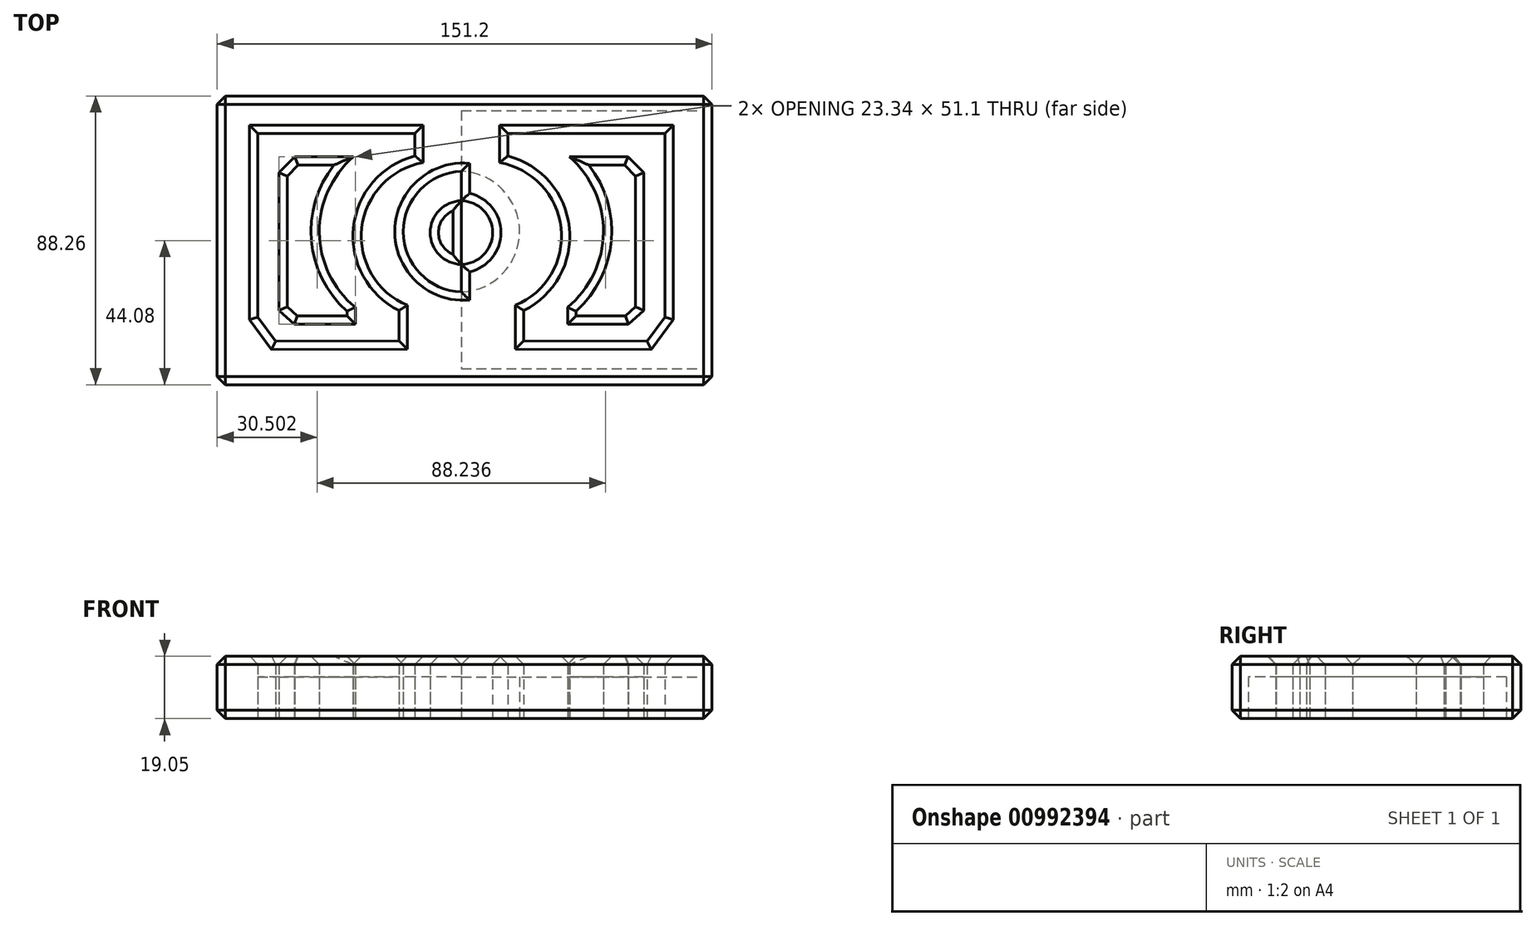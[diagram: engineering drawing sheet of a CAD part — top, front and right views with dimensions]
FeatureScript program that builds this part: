
annotation { "Feature Type Name" : "Feature", "Feature Type Description" : "" }
export const myFeature = defineFeature(function(context is Context, id is Id, definition is map)
    precondition{}
    {
        {
            var Q0;
            Q0=qCreatedBy(makeId("Top.planeOp"),FACE);
            var sketch = newSketch(context, id + "F0", { "sketchPlane" : qUnion([Q0])});
            skArc(sketch, "E0", {"start": v(0, 10.27) * mm, "mid": v(-9.53, 0.52) * mm, "end": v(0, -9.23) * mm});
            skArc(sketch, "E1", {"start": v(0, 19.24) * mm, "mid": v(-17.8, 0.8) * mm, "end": v(0, -17.63) * mm});
            skArc(sketch, "E2", {"start": v(-14.23, 23.93) * mm, "mid": v(-33, 1.98) * mm, "end": v(-19.07, -23.32) * mm});
            skArc(sketch, "E3", {"start": v(-33, 23.65) * mm, "mid": v(-43.41, 0.53) * mm, "end": v(-32.45, -22.32) * mm});
            skPoint(sketch, "E3.startSnap0", {"position": v(-33, 1.98) * mm});
            skLineSegment(sketch, "E4", {"start": v(-33, 23.65) * mm, "end": v(-50.95, 23.65) * mm});
            skLineSegment(sketch, "E5", {"start": v(-50.95, 23.65) * mm, "end": v(-55.79, 18.8) * mm});
            skLineSegment(sketch, "E6", {"start": v(-55.79, 18.8) * mm, "end": v(-55.79, 0) * mm});
            skLineSegment(sketch, "E7", {"start": v(-14.23, 23.93) * mm, "end": v(-14.23, 30.76) * mm});
            skLineSegment(sketch, "E8", {"start": v(-14.23, 30.76) * mm, "end": v(-62.2, 30.76) * mm});
            skLineSegment(sketch, "E9", {"start": v(-62.2, 30.76) * mm, "end": v(-62.2, -25.31) * mm});
            skLineSegment(sketch, "E10", {"start": v(-62.2, -25.31) * mm, "end": v(-58.64, -30.15) * mm});
            skLineSegment(sketch, "E11", {"start": v(-58.64, -30.15) * mm, "end": v(-56.78, -32.67) * mm});
            skLineSegment(sketch, "E12", {"start": v(-55.79, 0) * mm, "end": v(-55.79, -23.32) * mm});
            skLineSegment(sketch, "E13", {"start": v(-55.79, -23.32) * mm, "end": v(-51.1, -27.45) * mm});
            skLineSegment(sketch, "E14", {"start": v(-32.45, -22.32) * mm, "end": v(-32.45, -27.45) * mm});
            skLineSegment(sketch, "E15", {"start": v(0, 42.28) * mm, "end": v(0, -45.98) * mm});
            skPoint(sketch, "E15.endSnap0", {"position": v(1.57, -45.98) * mm});
            skLineSegment(sketch, "E16.MirrorCS", {"start": v(14.23, 30.76) * mm, "end": v(62.2, 30.76) * mm});
            skLineSegment(sketch, "E17.MirrorCS", {"start": v(14.23, 23.93) * mm, "end": v(14.23, 30.76) * mm});
            skArc(sketch, "E18.MirrorCS", {"start": v(14.23, 23.93) * mm, "mid": v(33, 1.98) * mm, "end": v(19.07, -23.32) * mm});
            skLineSegment(sketch, "E19.MirrorCS", {"start": v(62.2, -25.31) * mm, "end": v(58.64, -30.15) * mm});
            skLineSegment(sketch, "E20.MirrorCS", {"start": v(58.64, -30.15) * mm, "end": v(56.78, -32.67) * mm});
            skLineSegment(sketch, "E21.MirrorCS", {"start": v(62.2, 30.76) * mm, "end": v(62.2, -25.31) * mm});
            skLineSegment(sketch, "E22.MirrorCS", {"start": v(55.79, 0) * mm, "end": v(55.79, -23.32) * mm});
            skLineSegment(sketch, "E23.MirrorCS", {"start": v(55.79, 18.8) * mm, "end": v(55.79, 0) * mm});
            skLineSegment(sketch, "E24.MirrorCS", {"start": v(50.95, 23.65) * mm, "end": v(55.79, 18.8) * mm});
            skLineSegment(sketch, "E25.MirrorCS", {"start": v(33, 23.65) * mm, "end": v(50.95, 23.65) * mm});
            skArc(sketch, "E26.MirrorCS", {"start": v(33, 23.65) * mm, "mid": v(43.41, 0.53) * mm, "end": v(32.45, -22.32) * mm});
            skLineSegment(sketch, "E27.MirrorCS", {"start": v(32.45, -22.32) * mm, "end": v(32.45, -27.45) * mm});
            skLineSegment(sketch, "E28.MirrorCS", {"start": v(55.79, -23.32) * mm, "end": v(51.1, -27.45) * mm});
            skArc(sketch, "E29.MirrorCS", {"start": v(0, 19.24) * mm, "mid": v(17.8, 0.8) * mm, "end": v(0, -17.63) * mm});
            skArc(sketch, "E30.MirrorCS", {"start": v(0, 10.27) * mm, "mid": v(9.53, 0.52) * mm, "end": v(0, -9.23) * mm});
            skLineSegment(sketch, "E31.bottom", {"start": v(-70.02, 37.74) * mm, "end": v(73.73, 37.74) * mm});
            skLineSegment(sketch, "E31.top", {"start": v(-70.02, -41.11) * mm, "end": v(73.73, -41.11) * mm});
            skLineSegment(sketch, "E31.left", {"start": v(-70.02, 37.74) * mm, "end": v(-70.02, -41.11) * mm});
            skLineSegment(sketch, "E31.right", {"start": v(73.73, 37.74) * mm, "end": v(73.73, -41.11) * mm});
            skLineSegment(sketch, "E32.bottom", {"start": v(-74.62, 42.28) * mm, "end": v(76.58, 42.28) * mm});
            skLineSegment(sketch, "E32.top", {"start": v(-74.62, -45.98) * mm, "end": v(76.58, -45.98) * mm});
            skLineSegment(sketch, "E32.left", {"start": v(-74.62, 42.28) * mm, "end": v(-74.62, -45.98) * mm});
            skLineSegment(sketch, "E32.right", {"start": v(76.58, 42.28) * mm, "end": v(76.58, -45.98) * mm});
            skLineSegment(sketch, "E33", {"start": v(-51.1, -27.45) * mm, "end": v(-32.45, -27.45) * mm});
            skLineSegment(sketch, "E34", {"start": v(-19.07, -23.32) * mm, "end": v(-19.07, -32.53) * mm});
            skLineSegment(sketch, "E35", {"start": v(-19.07, -32.53) * mm, "end": v(-56.78, -32.67) * mm});
            skLineSegment(sketch, "E36.MirrorCS", {"start": v(51.1, -27.45) * mm, "end": v(32.45, -27.45) * mm});
            skLineSegment(sketch, "E37.MirrorCS", {"start": v(19.07, -32.53) * mm, "end": v(56.78, -32.67) * mm});
            skLineSegment(sketch, "E38.MirrorCS", {"start": v(19.07, -23.32) * mm, "end": v(19.07, -32.53) * mm});
            skSolve(sketch);
        }
        {
            var Q0;
            Q0=makeQuery(id+"F0.imprint","IMPRINT",FACE,{"disambiguationData":[TD([[makeQuery(id+"F0.imprint","IMPRINT",EDGE,{"derivedFrom":sQuery(id+"F0.wireOp",EDGE,"E3")}),-1.0]])]});
            var Q1;
            {var subQ5=sQuery(id+"F0.wireOp",EDGE,"E1");Q1=makeQuery(id+"F0.imprint","IMPRINT",FACE,{"disambiguationData":[TD([[makeQuery(id+"F0.imprint","IMPRINT",EDGE,{"derivedFrom":subQ5}),-1.0]])]});}
            var Q2;
            {var subQ0=sQuery(id+"F0.wireOp",EDGE,"E0");Q2=makeQuery(id+"F0.imprint","IMPRINT",FACE,{"disambiguationData":[TD([[makeQuery(id+"F0.imprint","IMPRINT",EDGE,{"derivedFrom":subQ0}),1.0]])]});}
            var Q3;
            {var subQ0=sQuery(id+"F0.wireOp",EDGE,"E30.MirrorCS");Q3=makeQuery(id+"F0.imprint","IMPRINT",FACE,{"disambiguationData":[TD([[makeQuery(id+"F0.imprint","IMPRINT",EDGE,{"derivedFrom":subQ0}),-1.0]])]});}
            var Q4;
            Q4=makeQuery(id+"F0.imprint","IMPRINT",FACE,{"disambiguationData":[TD([[makeQuery(id+"F0.imprint","IMPRINT",EDGE,{"derivedFrom":sQuery(id+"F0.wireOp",EDGE,"E16.MirrorCS")}),1.0]])]});
            var Q5;
            Q5=makeQuery(id+"F0.imprint","IMPRINT",FACE,{"disambiguationData":[TD([[makeQuery(id+"F0.imprint","IMPRINT",EDGE,{"derivedFrom":sQuery(id+"F0.wireOp",EDGE,"E22.MirrorCS")}),-1.0]])]});
            var Q6;
            {var subQ0=sQuery(id+"F0.wireOp",EDGE,"E31.left");Q6=makeQuery(id+"F0.imprint","IMPRINT",FACE,{"disambiguationData":[TD([[makeQuery(id+"F0.imprint","IMPRINT",EDGE,{"derivedFrom":subQ0}),-1.0]])]});}
            var Q7;
            {var subQ0=sQuery(id+"F0.wireOp",EDGE,"E31.right");Q7=makeQuery(id+"F0.imprint","IMPRINT",FACE,{"disambiguationData":[TD([[makeQuery(id+"F0.imprint","IMPRINT",EDGE,{"derivedFrom":subQ0}),1.0]])]});}
            extrude(context, id + "F1", {"entities" : qUnion([Q0, Q1, Q2, Q3, Q4, Q5, Q6, Q7]), "depth" : 19.05 * mm, "offsetDistance" : 25.4 * mm});
        }
        {
            var Q0;
            Q0=makeQuery(id+"F0.imprint","IMPRINT",FACE,{"disambiguationData":[TD([[makeQuery(id+"F0.imprint","IMPRINT",EDGE,{"derivedFrom":sQuery(id+"F0.wireOp",EDGE,"E16.MirrorCS")}),-1.0]])]});
            var Q1;
            {var subQ0=sQuery(id+"F0.wireOp",EDGE,"E0");Q1=makeQuery(id+"F0.imprint","IMPRINT",FACE,{"disambiguationData":[TD([[makeQuery(id+"F0.imprint","IMPRINT",EDGE,{"derivedFrom":subQ0}),-1.0]])]});}
            var Q2;
            {var subQ3=sQuery(id+"F0.wireOp",EDGE,"E29.MirrorCS");Q2=makeQuery(id+"F0.imprint","IMPRINT",FACE,{"disambiguationData":[TD([[makeQuery(id+"F0.imprint","IMPRINT",EDGE,{"derivedFrom":subQ3}),-1.0]])]});}
            var Q3;
            Q3=makeQuery(id+"F0.imprint","IMPRINT",FACE,{"disambiguationData":[TD([[makeQuery(id+"F0.imprint","IMPRINT",EDGE,{"derivedFrom":sQuery(id+"F0.wireOp",EDGE,"E2")}),-1.0]])]});
            extrude(context, id + "F2", {"entities" : qUnion([Q0, Q1, Q2, Q3]), "depth" : 12.7 * mm, "offsetDistance" : 25.4 * mm});
        }
        {
            var Q0;
            Q0=makeQuery(id+"F1.opExtrude","CAP_FACE",FACE,{"disambiguationData":[OSD([sQuery(id+"F0.wireOp",EDGE,"E1"),sQuery(id+"F0.wireOp",EDGE,"E2"),sQuery(id+"F0.wireOp",EDGE,"E7"),sQuery(id+"F0.wireOp",EDGE,"E8"),sQuery(id+"F0.wireOp",EDGE,"E9"),sQuery(id+"F0.wireOp",EDGE,"E10"),sQuery(id+"F0.wireOp",EDGE,"E11"),sQuery(id+"F0.wireOp",EDGE,"E16.MirrorCS"),sQuery(id+"F0.wireOp",EDGE,"E17.MirrorCS"),sQuery(id+"F0.wireOp",EDGE,"E19.MirrorCS"),sQuery(id+"F0.wireOp",EDGE,"E20.MirrorCS"),sQuery(id+"F0.wireOp",EDGE,"E21.MirrorCS"),sQuery(id+"F0.wireOp",EDGE,"E29.MirrorCS"),sQuery(id+"F0.wireOp",EDGE,"E18.MirrorCS"),sQuery(id+"F0.wireOp",EDGE,"E32.bottom"),sQuery(id+"F0.wireOp",EDGE,"E32.top"),sQuery(id+"F0.wireOp",EDGE,"E32.left"),sQuery(id+"F0.wireOp",EDGE,"E32.right"),sQuery(id+"F0.wireOp",EDGE,"E34"),sQuery(id+"F0.wireOp",EDGE,"E35"),sQuery(id+"F0.wireOp",EDGE,"E37.MirrorCS"),sQuery(id+"F0.wireOp",EDGE,"E38.MirrorCS")])],"isStart":false});
            var Q1;
            Q1=makeQuery(id+"F1.opExtrude","CAP_EDGE",EDGE,{"disambiguationData":[OSD([sQuery(id+"F0.wireOp",EDGE,"E6"),sQuery(id+"F0.wireOp",EDGE,"E12")])],"isStart":false});
            var Q2;
            Q2=makeQuery(id+"F1.opExtrude","CAP_FACE",FACE,{"disambiguationData":[OSD([sQuery(id+"F0.wireOp",EDGE,"E3"),sQuery(id+"F0.wireOp",EDGE,"E4"),sQuery(id+"F0.wireOp",EDGE,"E5"),sQuery(id+"F0.wireOp",EDGE,"E6"),sQuery(id+"F0.wireOp",EDGE,"E12"),sQuery(id+"F0.wireOp",EDGE,"E13"),sQuery(id+"F0.wireOp",EDGE,"E14"),sQuery(id+"F0.wireOp",EDGE,"E33")])],"isStart":false});
            var Q3;
            Q3=makeQuery(id+"F1.opExtrude","CAP_FACE",FACE,{"disambiguationData":[OSD([sQuery(id+"F0.wireOp",EDGE,"E22.MirrorCS"),sQuery(id+"F0.wireOp",EDGE,"E23.MirrorCS"),sQuery(id+"F0.wireOp",EDGE,"E24.MirrorCS"),sQuery(id+"F0.wireOp",EDGE,"E25.MirrorCS"),sQuery(id+"F0.wireOp",EDGE,"E26.MirrorCS"),sQuery(id+"F0.wireOp",EDGE,"E27.MirrorCS"),sQuery(id+"F0.wireOp",EDGE,"E28.MirrorCS"),sQuery(id+"F0.wireOp",EDGE,"E36.MirrorCS")])],"isStart":false});
            var Q4;
            Q4=makeQuery(id+"F1.opExtrude","CAP_FACE",FACE,{"disambiguationData":[OSD([sQuery(id+"F0.wireOp",EDGE,"E0"),sQuery(id+"F0.wireOp",EDGE,"E30.MirrorCS")])],"isStart":false});
            var Q5;
            Q5=makeQuery(id+"F1.opExtrude","SWEPT_FACE",FACE,{"disambiguationData":[OSD([sQuery(id+"F0.wireOp",EDGE,"E32.top")])]});
            var Q6;
            Q6=makeQuery(id+"F1.opExtrude","SWEPT_FACE",FACE,{"disambiguationData":[OSD([sQuery(id+"F0.wireOp",EDGE,"E32.left")])]});
            var Q7;
            Q7=makeQuery(id+"F1.opExtrude","SWEPT_FACE",FACE,{"disambiguationData":[OSD([sQuery(id+"F0.wireOp",EDGE,"E32.right")])]});
            var Q8;
            Q8=makeQuery(id+"F1.opExtrude","SWEPT_FACE",FACE,{"disambiguationData":[OSD([sQuery(id+"F0.wireOp",EDGE,"E32.bottom")])]});
            chamfer(context, id + "F3", {"entities" : qUnion([Q0, Q1, Q2, Q3, Q4, Q5, Q6, Q7, Q8]), "width" : 2.54 * mm, "tangentPropagation" : true});
        }
    });
